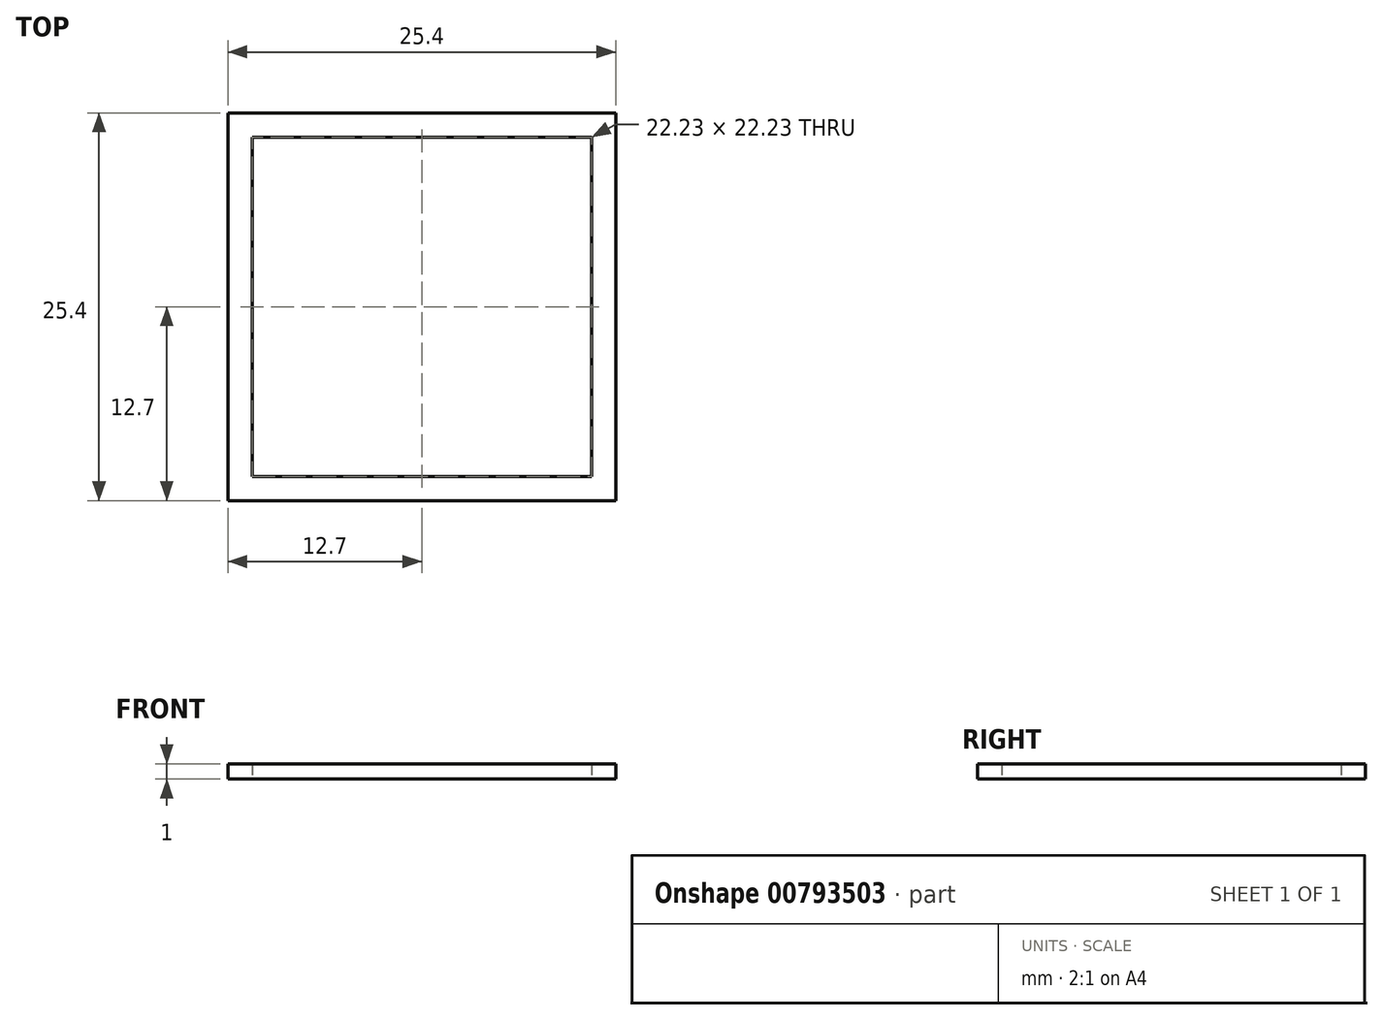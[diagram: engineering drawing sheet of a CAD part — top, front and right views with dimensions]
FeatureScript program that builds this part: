
annotation { "Feature Type Name" : "Feature", "Feature Type Description" : "" }
export const myFeature = defineFeature(function(context is Context, id is Id, definition is map)
    precondition{}
    {
        {
            assignVariable(context, id + "F0", {"name" : "Length", "anyValue" : 1});
        }
        {
            var Q0;
            Q0=qCreatedBy(makeId("Top.planeOp"),FACE);
            var sketch = newSketch(context, id + "F1", { "sketchPlane" : qUnion([Q0])});
            skLineSegment(sketch, "E0.bottom", {"start": v(-12.7, 12.7) * mm, "end": v(12.7, 12.7) * mm});
            skLineSegment(sketch, "E0.top", {"start": v(-12.7, -12.7) * mm, "end": v(12.7, -12.7) * mm});
            skLineSegment(sketch, "E0.left", {"start": v(-12.7, 12.7) * mm, "end": v(-12.7, -12.7) * mm});
            skLineSegment(sketch, "E0.right", {"start": v(12.7, 12.7) * mm, "end": v(12.7, -12.7) * mm});
            skPoint(sketch, "E0.middle", {"position": v(0, 0) * mm});
            skLineSegment(sketch, "E1.0", {"start": v(-11.11, 11.11) * mm, "end": v(11.11, 11.11) * mm});
            skLineSegment(sketch, "E1.1", {"start": v(-11.11, 11.11) * mm, "end": v(-11.11, -11.11) * mm});
            skLineSegment(sketch, "E1.2", {"start": v(-11.11, -11.11) * mm, "end": v(11.11, -11.11) * mm});
            skLineSegment(sketch, "E1.3", {"start": v(11.11, 11.11) * mm, "end": v(11.11, -11.11) * mm});
            skSolve(sketch);
        }
        {
            var Q0;
            Q0=makeQuery(id+"F1.imprint","IMPRINT",FACE,{"disambiguationData":[TD([[makeQuery(id+"F1.imprint","IMPRINT",EDGE,{"derivedFrom":sQuery(id+"F1.wireOp",EDGE,"E0.bottom")}),-1.0]])]});
            extrude(context, id + "F2", {"entities" : qUnion([Q0]), "depth" : (getVariable(context, 'Length')) * mm, "offsetDistance" : 25.4 * mm});
        }
    });
